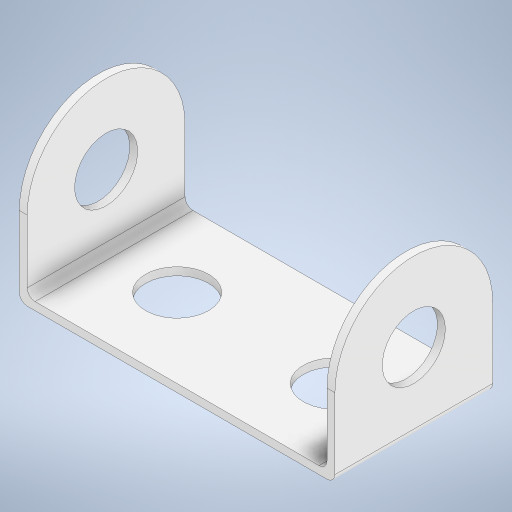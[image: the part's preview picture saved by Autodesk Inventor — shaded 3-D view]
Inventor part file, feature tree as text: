
AUTODESK INVENTOR PART (.ipt)
format: ipt  version: 2024 (Build 280153000, 153)  size: 296,960 bytes
history: native  units: mm
features: extrude x4, sketch x4, pattern_linear x2, fillet x2, other x1
ambient origin geometry x8: Origin, YZ Plane, XZ Plane, XY Plane, X Axis, Y Axis, Z Axis, Center Point
bodies: Body1 (feature_tree)
feature tree (13):
  other  "Těleso1"
  extrude  "Vysunutí1"  Depth=10.0mm
  extrude  "Vysunutí2"  Depth=10.0mm
  pattern_linear  "Obdélníkové pole1"  Spacing1=0.5mm  [1 undecoded]
  extrude  "Vysunutí3"  Depth=0.5mm
  pattern_linear  "Obdélníkové pole2"  Spacing1=0.5mm  [1 undecoded]
  extrude  "Vysunutí4"  Depth=10.0mm
  fillet  "Zaoblení1"  Radius=10.0mm
  fillet  "Zaoblení2"  Radius=10.0mm
  sketch  "Náčrt1"
  sketch  "Náčrt2"
  sketch  "Náčrt3"
  sketch  "Náčrt4"
note: 2 required parameter values undecoded (feature->parameter linkage not recoverable at this tier; creation-order binding heuristic only, values carry confidence <= 0.55)
